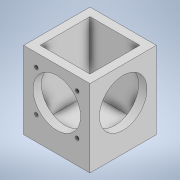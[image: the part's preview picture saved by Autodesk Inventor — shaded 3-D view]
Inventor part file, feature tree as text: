
AUTODESK INVENTOR PART (.ipt)
format: ipt  version: 2021 (Build 250183000, 183)  size: 137,728 bytes
history: native  units: mm
features: sketch x6, extrude x4, hole x2
ambient origin geometry x8: Origin, YZ Plane, XZ Plane, XY Plane, X Axis, Y Axis, Z Axis, Center Point
bodies: Solid1 (feature_tree)
feature tree (12):
  extrude  "Extrusion1"  Depth=60.0mm
  extrude  "Extrusion2"  Depth=45.0mm
  extrude  "Extrusion3"  Depth=60.0mm TaperAngle=0.0deg
  extrude  "Extrusion4"  Depth=15.0mm TaperAngle=0.0deg
  hole  "Hole1"  [1 undecoded]
  hole  "Hole2"  [1 undecoded]
  sketch  "Sketch1"  dims[d0=60.0mm d1=60.0mm]
  sketch  "Sketch2"  dims[d2=70.0mm d3=0.0mm d4=45.0mm]
  sketch  "Sketch3"  dims[d5=45.0mm d6=60.0mm d7=0.0mm]
  sketch  "Sketch4"  dims[d8=43.0mm d9=15.0mm d10=0.0mm]
  sketch  "Sketch5"  dims[d11=43.0mm d12=15.0mm d13=0.0mm]
  sketch  "Sketch7"  dims[d14=3.302mm d15=6.0mm d16=7.938mm d17=4.166mm d18=90.0deg d19=8.0mm d20=0.0mm d21=37.0mm d22=37.0mm d23=3.302mm d24=5.0mm d25=7.938mm d26=4.166mm d27=90.0deg d28=6.0mm d29=0.0mm]
note: 2 required parameter values undecoded (feature->parameter linkage not recoverable at this tier; creation-order binding heuristic only, values carry confidence <= 0.55)
